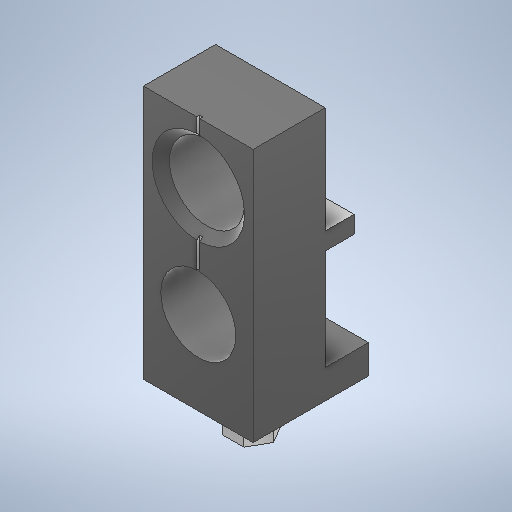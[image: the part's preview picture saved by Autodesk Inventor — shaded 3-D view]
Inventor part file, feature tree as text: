
AUTODESK INVENTOR PART (.ipt)
format: ipt  version: 2025.3 (Build 293356000, 356)  size: 297,984 bytes
history: native  units: mm
features: extrude x5, sketch x3, other x1, chamfer x1
ambient origin geometry x8: Origin, YZ Plane, XZ Plane, XY Plane, X Axis, Y Axis, Z Axis, Center Point
bodies: Body1 (feature_tree)
feature tree (10):
  other  "ソリッド1"
  extrude  "スペーサ"  Depth=7.6mm
  sketch  "スケッチ2"
  extrude  "押し出し2"  TaperAngle=0.0deg  [1 undecoded]
  extrude  "押し出し5"  Depth=5.8mm
  chamfer  "面取り1"  Distance=2.0mm
  extrude  "足"  Depth=1.2mm
  extrude  "押し出し6"  Depth=3.0mm TaperAngle=0.0deg
  sketch  "スケッチ1"
  sketch  "スケッチ5"
note: 1 required parameter value undecoded (feature->parameter linkage not recoverable at this tier; creation-order binding heuristic only, values carry confidence <= 0.55)
